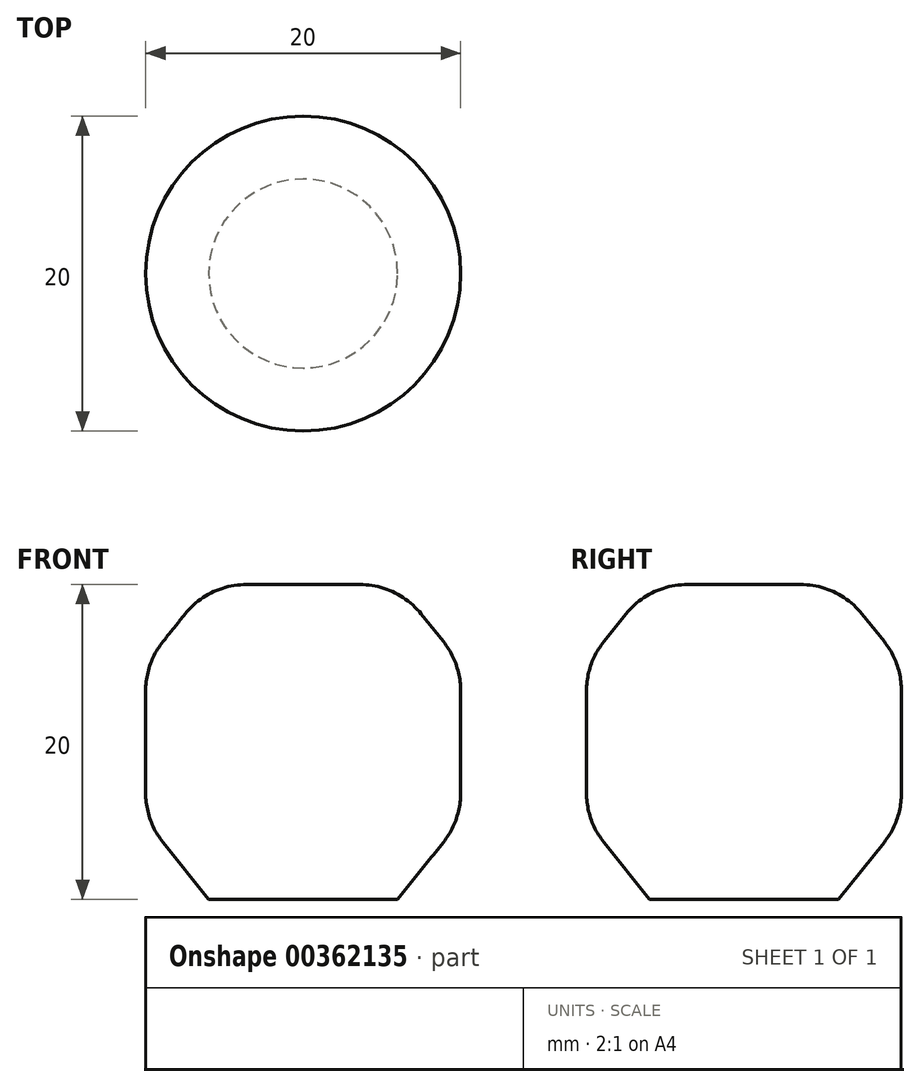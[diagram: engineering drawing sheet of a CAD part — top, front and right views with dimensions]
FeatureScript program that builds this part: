
annotation { "Feature Type Name" : "Feature", "Feature Type Description" : "" }
export const myFeature = defineFeature(function(context is Context, id is Id, definition is map)
    precondition{}
    {
        {
            var Q0;
            Q0=qCreatedBy(makeId("Top.planeOp"),FACE);
            var sketch = newSketch(context, id + "F0", { "sketchPlane" : qUnion([Q0])});
            skCircle(sketch, "E0", {"center": v(0, 0) * mm, "radius": 10 * mm});
            skSolve(sketch);
        }
        {
            var Q0;
            Q0=makeQuery(id+"F0.imprint","IMPRINT",FACE,{"disambiguationData":[TD([[makeQuery(id+"F0.imprint","IMPRINT",EDGE,{"derivedFrom":sQuery(id+"F0.wireOp",EDGE,"E0")}),1.0]])]});
            extrude(context, id + "F1", {"entities" : qUnion([Q0]), "depth" : 20 * mm, "offsetDistance" : 25 * mm});
        }
        {
            var Q0;
            Q0=makeQuery(id+"F1.opExtrude","CAP_EDGE",EDGE,{"disambiguationData":[OSD([sQuery(id+"F0.wireOp",EDGE,"E0")])],"isStart":false});
            var Q1;
            Q1=makeQuery(id+"F1.opExtrude","CAP_EDGE",EDGE,{"disambiguationData":[OSD([sQuery(id+"F0.wireOp",EDGE,"E0")])],"isStart":true});
            chamfer(context, id + "F2", {"entities" : qUnion([Q0, Q1]), "chamferType" : ChamferType.TWO_OFFSETS, "width1" : 4 * mm, "oppositeDirection" : false, "width2" : 5 * mm, "tangentPropagation" : true});
        }
        {
            var Q0;
            {var subQ0=sQuery(id+"F0.wireOp",EDGE,"E0");Q0=makeQuery(id+"F2.opChamfer","BLEND_EDGE",EDGE,{"blendedFrom":[makeQuery(id+"F1.opExtrude","CAP_EDGE",EDGE,{"disambiguationData":[OSD([subQ0])],"isStart":false}),makeQuery(id+"F1.opExtrude","SWEPT_FACE",FACE,{"disambiguationData":[OSD([subQ0])]})],"blendedInto":[makeQuery(id+"F1.opExtrude","SWEPT_FACE",FACE,{"disambiguationData":[OSD([subQ0])]})]});}
            var Q1;
            {var subQ0=sQuery(id+"F0.wireOp",EDGE,"E0");Q1=makeQuery(id+"F2.opChamfer","BLEND_EDGE",EDGE,{"blendedFrom":[makeQuery(id+"F1.opExtrude","CAP_EDGE",EDGE,{"disambiguationData":[OSD([subQ0])],"isStart":false}),makeQuery(id+"F1.opExtrude","CAP_FACE",FACE,{"disambiguationData":[OSD([subQ0])],"isStart":false})],"blendedInto":[makeQuery(id+"F1.opExtrude","CAP_FACE",FACE,{"disambiguationData":[OSD([subQ0])],"isStart":false})]});}
            var Q2;
            {var subQ0=sQuery(id+"F0.wireOp",EDGE,"E0");Q2=makeQuery(id+"F2.opChamfer","BLEND_EDGE",EDGE,{"blendedFrom":[makeQuery(id+"F1.opExtrude","CAP_EDGE",EDGE,{"disambiguationData":[OSD([subQ0])],"isStart":true}),makeQuery(id+"F1.opExtrude","SWEPT_FACE",FACE,{"disambiguationData":[OSD([subQ0])]})],"blendedInto":[makeQuery(id+"F1.opExtrude","SWEPT_FACE",FACE,{"disambiguationData":[OSD([subQ0])]})]});}
            fillet(context, id + "F3", {"entities" : qUnion([Q0, Q1, Q2]), "tangentPropagation" : true, "radius" : 5 * mm, "defaultsChanged" : false, "vertexSettings" : [], "allowEdgeOverflow" : false});
        }
    });
